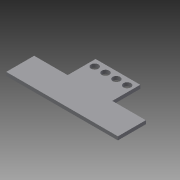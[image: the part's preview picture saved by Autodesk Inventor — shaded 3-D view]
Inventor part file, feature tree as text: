
AUTODESK INVENTOR PART (.ipt)
format: ipt  version: 2013 (Build 170138000, 138)  size: 84,992 bytes
history: native  units: in
note: dims shown in document units (in); Inventor stores cm internally (conversion verified against a paired STEP export)
features: extrude x1, sketch x1
ambient origin geometry x8: Origin, YZ Plane, XZ Plane, XY Plane, X Axis, Y Axis, Z Axis, Center Point
bodies: Solid1 (feature_tree)
feature tree (2):
  extrude  "Extrusion1"  Depth=0.8in
  sketch  "Sketch1"  dims[d4=0.8in d5=0.8in d6=1.0in d7=1.2in d8=1.0in d9=4.0in d10=1.2in d11=0.125in d12=0.0in]
